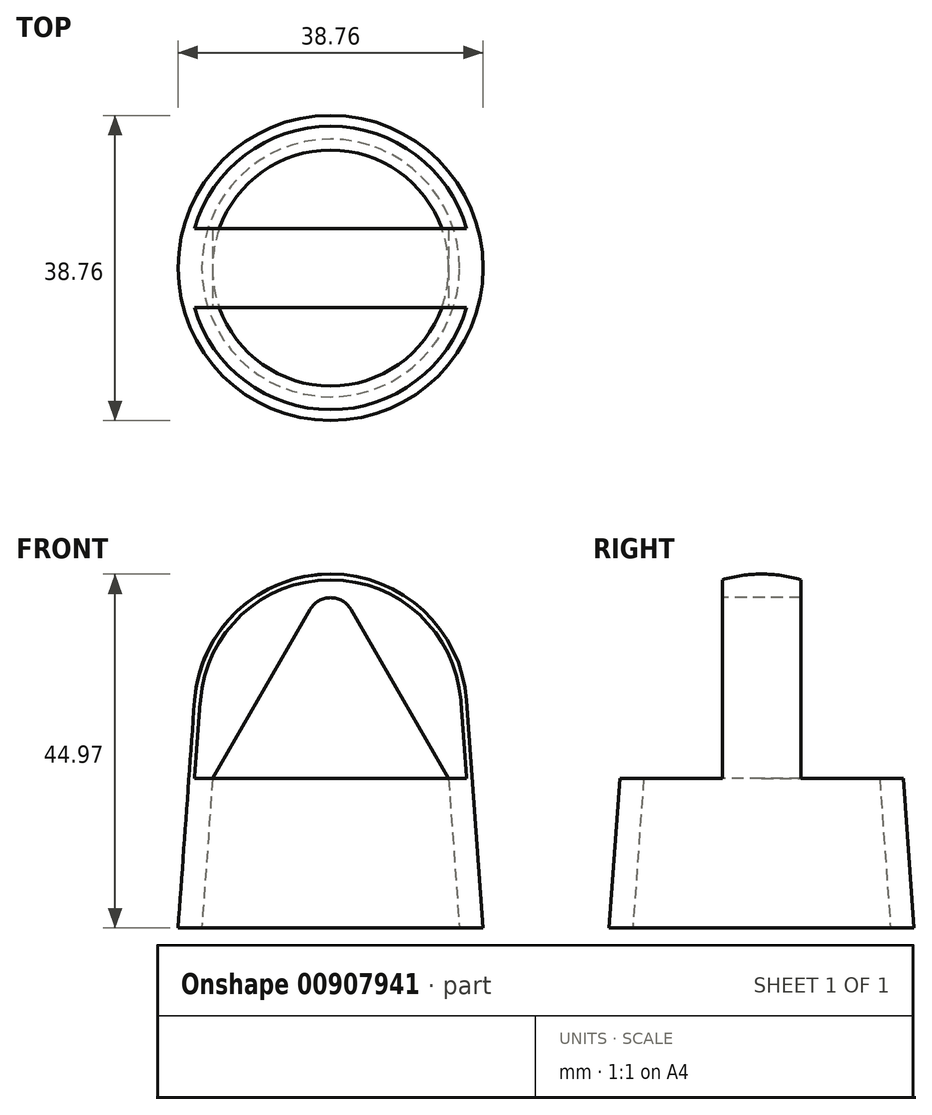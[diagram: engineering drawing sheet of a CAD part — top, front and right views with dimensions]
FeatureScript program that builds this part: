
annotation { "Feature Type Name" : "Feature", "Feature Type Description" : "" }
export const myFeature = defineFeature(function(context is Context, id is Id, definition is map)
    precondition{}
    {
        {
            var Q0;
            Q0=qCreatedBy(makeId("Front.planeOp"),FACE);
            var sketch = newSketch(context, id + "F0", { "sketchPlane" : qUnion([Q0])});
            skLineSegment(sketch, "E0", {"start": v(-19.38, 0) * mm, "end": v(-18, 19) * mm});
            skLineSegment(sketch, "E1", {"start": v(0, 44.97) * mm, "end": v(0, 41.97) * mm});
            skLineSegment(sketch, "E2", {"start": v(-15, 19) * mm, "end": v(0, 19) * mm});
            skLineSegment(sketch, "E3", {"start": v(-18, 19) * mm, "end": v(-17.28, 28.89) * mm});
            skLineSegment(sketch, "E4", {"start": v(-19.38, 0) * mm, "end": v(-16.37, 0) * mm});
            skLineSegment(sketch, "E5", {"start": v(-16.37, 0) * mm, "end": v(0, 0) * mm, "construction": true});
            skLineSegment(sketch, "E6", {"start": v(-2.6, 40.47) * mm, "end": v(-15, 19) * mm});
            skLineSegment(sketch, "E7", {"start": v(-16.37, 0) * mm, "end": v(-15, 19) * mm});
            skArc(sketch, "E8", {"start": v(-17.28, 28.89) * mm, "mid": v(-11.8, 40.33) * mm, "end": v(0, 44.97) * mm});
            skLineSegment(sketch, "E9", {"start": v(0, 44.97) * mm, "end": v(0, 44.97) * mm});
            skLineSegment(sketch, "E10", {"start": v(0, 19) * mm, "end": v(0, 41.97) * mm});
            skPoint(sketch, "E11.orphan", {"position": v(0, 267.73) * mm});
            skLineSegment(sketch, "E12.MirrorCS", {"start": v(2.6, 40.47) * mm, "end": v(15, 19) * mm});
            skLineSegment(sketch, "E13.MirrorCS", {"start": v(15, 19) * mm, "end": v(0, 19) * mm});
            skPoint(sketch, "E14.visualSharp", {"position": v(15, 19) * mm});
            skArc(sketch, "E15", {"start": v(2.6, 40.47) * mm, "mid": v(1.5, 41.57) * mm, "end": v(0, 41.97) * mm});
            skLineSegment(sketch, "E16.trimOffspring", {"start": v(0, 41.97) * mm, "end": v(0, 0) * mm, "construction": true});
            skPoint(sketch, "E17.orphan", {"position": v(0, 44.97) * mm});
            skArc(sketch, "E18", {"start": v(0, 41.97) * mm, "mid": v(-1.5, 41.57) * mm, "end": v(-2.6, 40.47) * mm});
            skSolve(sketch);
        }
        {
            var Q0;
            {var subQ4=sQuery(id+"F0.wireOp",EDGE,"E1");Q0=makeQuery(id+"F0.imprint","IMPRINT",FACE,{"disambiguationData":[TD([[makeQuery(id+"F0.imprint","IMPRINT",EDGE,{"derivedFrom":subQ4}),-1.0]])]});}
            var Q1;
            {var subQ1=sQuery(id+"F0.wireOp",EDGE,"E0");Q1=makeQuery(id+"F0.imprint","IMPRINT",FACE,{"disambiguationData":[TD([[makeQuery(id+"F0.imprint","IMPRINT",EDGE,{"derivedFrom":subQ1}),-1.0]])]});}
            var Q2;
            Q2=sQuery(id+"F0.wireOp",EDGE,"E10");
            revolve(context, id + "F1", {"surfaceOperationType" : NewSurfaceOperationType.NEW, "entities" : qUnion([Q0, Q1]), "axis" : qUnion([Q2]), "revolveType" : RevolveType.FULL});
        }
        {
            var Q0;
            Q0=qCreatedBy(makeId("Right.planeOp"),FACE);
            var sketch = newSketch(context, id + "F2", { "sketchPlane" : qUnion([Q0])});
            skLineSegment(sketch, "E19.bottom", {"start": v(-45, 44.97) * mm, "end": v(-5, 44.97) * mm});
            skLineSegment(sketch, "E19.top", {"start": v(-45, 19) * mm, "end": v(-5, 19) * mm});
            skLineSegment(sketch, "E19.left", {"start": v(-45, 44.97) * mm, "end": v(-45, 19) * mm});
            skLineSegment(sketch, "E19.right", {"start": v(-5, 44.97) * mm, "end": v(-5, 19) * mm});
            skLineSegment(sketch, "E20.MirrorCS", {"start": v(45, 44.97) * mm, "end": v(45, 19) * mm});
            skLineSegment(sketch, "E21.MirrorCS", {"start": v(45, 19) * mm, "end": v(5, 19) * mm});
            skLineSegment(sketch, "E22.MirrorCS", {"start": v(45, 44.97) * mm, "end": v(5, 44.97) * mm});
            skLineSegment(sketch, "E23.MirrorCS", {"start": v(5, 44.97) * mm, "end": v(5, 19) * mm});
            skLineSegment(sketch, "E24", {"start": v(-5, 44.97) * mm, "end": v(0, 44.97) * mm, "construction": true});
            skLineSegment(sketch, "E25", {"start": v(0, 44.97) * mm, "end": v(5, 44.97) * mm, "construction": true});
            skSolve(sketch);
        }
        {
            var Q0;
            Q0 = qSketchRegion(id + "F2", true);
            extrude(context, id + "F3", {"entities" : qUnion([Q0]), "operationType" : NewBodyOperationType.REMOVE, "endBound" : BoundingType.THROUGH_ALL, "depth" : 25 * mm, "offsetDistance" : 25 * mm, "hasSecondDirection" : true, "secondDirectionBound" : SecondDirectionBoundingType.THROUGH_ALL, "secondDirectionOppositeDirection" : true, "secondDirectionDepth" : 25 * mm});
        }
        {
            var Q0;
            Q0=makeQuery(id+"F0.imprint","IMPRINT",FACE,{"disambiguationData":[TD([[makeQuery(id+"F0.imprint","IMPRINT",EDGE,{"derivedFrom":sQuery(id+"F0.wireOp",EDGE,"E2")}),1.0]])]});
            var Q1;
            Q1=makeQuery(id+"F0.imprint","IMPRINT",FACE,{"disambiguationData":[TD([[makeQuery(id+"F0.imprint","IMPRINT",EDGE,{"derivedFrom":sQuery(id+"F0.wireOp",EDGE,"E10")}),-1.0]])]});
            extrude(context, id + "F4", {"entities" : qUnion([Q0, Q1]), "operationType" : NewBodyOperationType.REMOVE, "endBound" : BoundingType.THROUGH_ALL, "oppositeDirection" : true, "depth" : 25 * mm, "offsetDistance" : 25 * mm, "hasSecondDirection" : true, "secondDirectionBound" : SecondDirectionBoundingType.THROUGH_ALL, "secondDirectionOppositeDirection" : false, "secondDirectionDepth" : 25 * mm});
        }
    });
